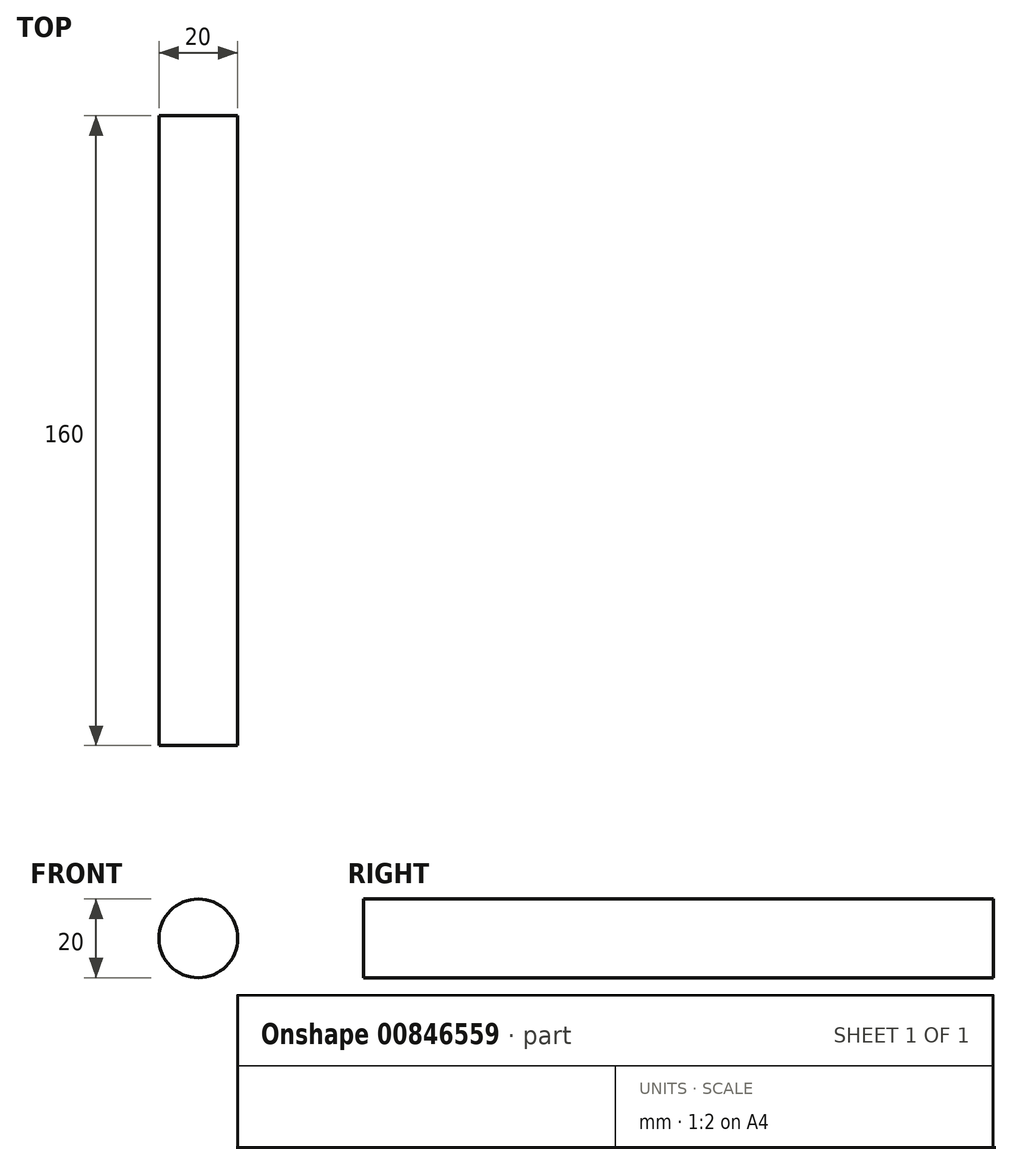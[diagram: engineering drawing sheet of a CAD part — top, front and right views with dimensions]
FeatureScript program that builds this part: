
annotation { "Feature Type Name" : "Feature", "Feature Type Description" : "" }
export const myFeature = defineFeature(function(context is Context, id is Id, definition is map)
    precondition{}
    {
        {
            var Q0;
            Q0=qCreatedBy(makeId("Front.planeOp"),FACE);
            var sketch = newSketch(context, id + "F0", { "sketchPlane" : qUnion([Q0])});
            skCircle(sketch, "E0", {"center": v(0, 0) * mm, "radius": 10 * mm});
            skSolve(sketch);
        }
        {
            var Q0;
            Q0 = qSketchRegion(id + "F0", true);
            extrude(context, id + "F1", {"entities" : qUnion([Q0]), "depth" : 160 * mm, "offsetDistance" : 25 * mm});
        }
    });
